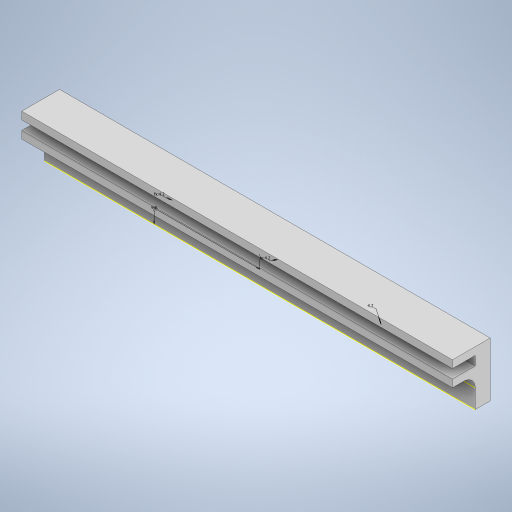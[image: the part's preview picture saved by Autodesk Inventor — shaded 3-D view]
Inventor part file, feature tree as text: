
AUTODESK INVENTOR PART (.ipt)
format: ipt  version: 2023 (Build 270158000, 158)  size: 300,544 bytes
history: native  units: in
note: dims shown in document units (in); Inventor stores cm internally (conversion verified against a paired STEP export)
features: sketch x4, extrude x3, hole x3, fillet x1
ambient origin geometry x8: Origin, YZ Plane, XZ Plane, XY Plane, X Axis, Y Axis, Z Axis, Center Point
bodies: Solid1 (feature_tree)
feature tree (11):
  extrude  "Extrusion1"  Depth=1.4173in
  extrude  "Extrusion2"  Depth=0.1969in
  extrude  "Extrusion3"  Depth=0.1969in
  fillet  "Fillet1"  Radius=0.5906in
  hole  "Hole1"  [1 undecoded]
  hole  "Hole2"  [1 undecoded]
  hole  "Hole3"  [1 undecoded]
  sketch  "Sketch11"  dims[d9=11.2205in d10=0.1969in d11=0.5906in d12=0.0in d13=0.2953in d15=0.1969in d16=0.2362in d17=0.1575in d18=0.0787in d19=90.0deg d20=0.315in d21=0.8108in d23=0.1969in d24=0.1969in d25=0.2362in d26=0.1575in d27=0.0787in d28=90.0deg d29=0.315in d30=0.8108in d31=0.1969in d32=0.1969in d33=0.2362in d34=0.1575in d35=0.0787in d36=90.0deg d37=0.315in d38=0.8108in d39=2.7559in d43=0.374in d47=0.4331in d48=0.2756in d50=2.7559in d51=0.374in d52=0.1654in d53=0.1654in d54=0.1654in d14=0.0in]
  sketch  "Sketch1"  dims[d0=11.2205in d1=1.4173in]
  sketch  "Sketch4"  dims[d2=0.3937in d3=0.0in d4=0.1969in]
  sketch  "Sketch5"  dims[d5=11.2205in d6=0.1969in d7=0.5906in d8=0.0in]
note: 3 required parameter values undecoded (feature->parameter linkage not recoverable at this tier; creation-order binding heuristic only, values carry confidence <= 0.55)
